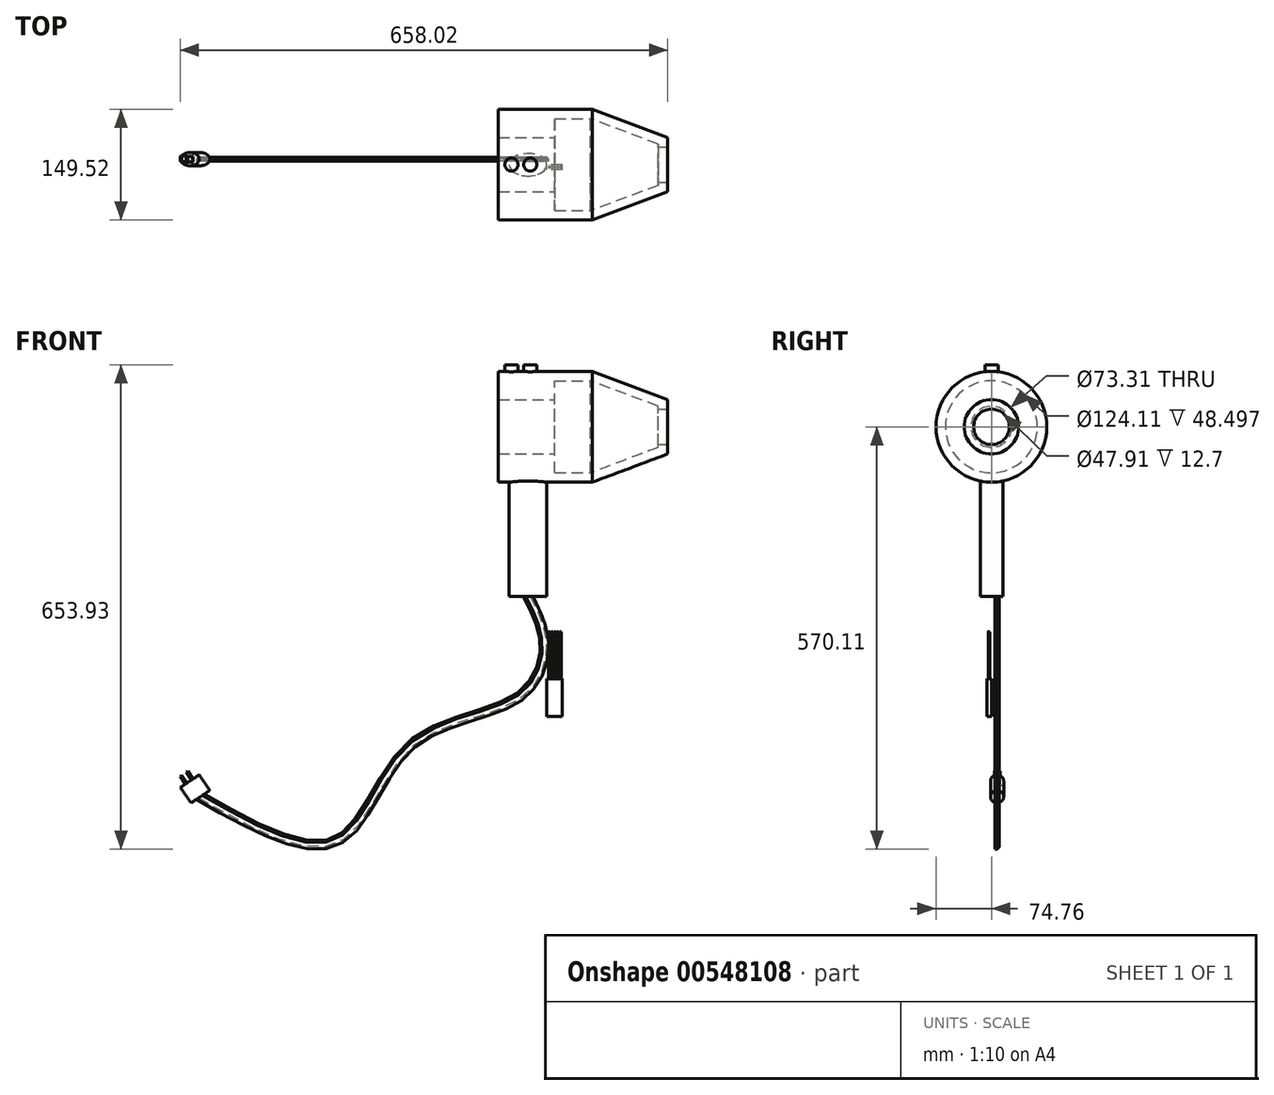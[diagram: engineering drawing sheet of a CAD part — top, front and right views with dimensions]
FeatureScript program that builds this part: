
annotation { "Feature Type Name" : "Feature", "Feature Type Description" : "" }
export const myFeature = defineFeature(function(context is Context, id is Id, definition is map)
    precondition{}
    {
        {
            var Q0;
            Q0=qCreatedBy(makeId("Front.planeOp"),FACE);
            var sketch = newSketch(context, id + "F0", { "sketchPlane" : qUnion([Q0])});
            skLineSegment(sketch, "E0", {"start": v(-65.57, 36.66) * mm, "end": v(-65.57, 74.76) * mm});
            skLineSegment(sketch, "E1", {"start": v(-65.57, 74.76) * mm, "end": v(61.43, 74.76) * mm});
            skLineSegment(sketch, "E2", {"start": v(61.43, 74.76) * mm, "end": v(163.03, 36.66) * mm});
            skLineSegment(sketch, "E3", {"start": v(163.03, 36.66) * mm, "end": v(163.03, 23.96) * mm});
            skLineSegment(sketch, "E4", {"start": v(163.03, 23.96) * mm, "end": v(150.33, 23.96) * mm});
            skLineSegment(sketch, "E5", {"start": v(150.33, 23.96) * mm, "end": v(150.33, 27.86) * mm});
            skLineSegment(sketch, "E6", {"start": v(150.33, 27.86) * mm, "end": v(59.13, 62.06) * mm});
            skLineSegment(sketch, "E7", {"start": v(59.13, 62.06) * mm, "end": v(10.63, 62.06) * mm});
            skLineSegment(sketch, "E8", {"start": v(10.63, 62.06) * mm, "end": v(10.63, 36.66) * mm});
            skLineSegment(sketch, "E9", {"start": v(10.63, 36.66) * mm, "end": v(-65.57, 36.66) * mm});
            skLineSegment(sketch, "E10", {"start": v(0, 0) * mm, "end": v(-123.38, 0) * mm, "construction": true});
            skSolve(sketch);
        }
        {
            var Q0;
            Q0=makeQuery(id+"F0.imprint","IMPRINT",FACE,{"disambiguationData":[TD([[makeQuery(id+"F0.imprint","IMPRINT",EDGE,{"derivedFrom":sQuery(id+"F0.wireOp",EDGE,"E0")}),-1.0]])]});
            var Q1;
            Q1=sQuery(id+"F0.wireOp",EDGE,"E10");
            revolve(context, id + "F1", {"entities" : qUnion([Q0]), "axis" : qUnion([Q1]), "revolveType" : RevolveType.FULL});
        }
        {
            var Q0;
            Q0=qCreatedBy(makeId("Top.planeOp"),FACE);
            cPlane(context, id + "F2", {"entities" : qUnion([Q0]), "cplaneType" : CPlaneType.OFFSET, "offset" : 50.8 * mm, "oppositeDirection" : true, "width" : 152.4 * mm, "height" : 152.4 * mm});
        }
        {
            var Q0;
            Q0=qCreatedBy(id+"F2.planeOp",FACE);
            var sketch = newSketch(context, id + "F3", { "sketchPlane" : qUnion([Q0])});
            skLineSegment(sketch, "E11", {"start": v(-43.6, 0) * mm, "end": v(0, 0) * mm});
            skEllipse(sketch, "E12", {"center": v(-25.4, 0) * mm, "majorRadius": 25.4 * mm, "minorRadius": 15.24 * mm, "majorAxis": v(1, 0)});
            skSolve(sketch);
        }
        {
            var Q0;
            Q0 = qSketchRegion(id + "F3", true);
            extrude(context, id + "F4", {"entities" : qUnion([Q0]), "operationType" : NewBodyOperationType.ADD, "oppositeDirection" : true, "depth" : 177.8 * mm, "offsetDistance" : 25.4 * mm});
        }
        {
            var Q0;
            Q0=makeQuery(id+"F4.opExtrude","CAP_FACE",FACE,{"disambiguationData":[OSD([sQuery(id+"F3.wireOp",EDGE,"E12")])],"isStart":false});
            var sketch = newSketch(context, id + "F5", { "sketchPlane" : qUnion([Q0])});
            skLineSegment(sketch, "E13", {"start": v(-7.37, -7.62) * mm, "end": v(-43.43, -7.62) * mm, "construction": true});
            skLineSegment(sketch, "E14.bottom", {"start": v(-31.75, -10.22) * mm, "end": v(-19.05, -10.22) * mm});
            skLineSegment(sketch, "E14.top", {"start": v(-31.75, -5.02) * mm, "end": v(-19.05, -5.02) * mm});
            skLineSegment(sketch, "E14.left", {"start": v(-31.75, -10.22) * mm, "end": v(-31.75, -5.02) * mm});
            skLineSegment(sketch, "E14.right", {"start": v(-19.05, -10.22) * mm, "end": v(-19.05, -5.02) * mm});
            skPoint(sketch, "E14.middle", {"position": v(-25.4, -7.62) * mm});
            skLineSegment(sketch, "E15", {"start": v(-50.8, 0) * mm, "end": v(0, 0) * mm, "construction": true});
            skLineSegment(sketch, "E16", {"start": v(-25.4, -15.24) * mm, "end": v(-25.4, 15.24) * mm, "construction": true});
            skEllipse(sketch, "E17", {"center": v(-25.4, -7.62) * mm, "majorRadius": 7.62 * mm, "minorRadius": 3.81 * mm, "majorAxis": v(0.9, 0.42)});
            skSolve(sketch);
        }
        {
            var Q0;
            Q0=qCreatedBy(makeId("Front.planeOp"),FACE);
            cPlane(context, id + "F6", {"entities" : qUnion([Q0]), "cplaneType" : CPlaneType.OFFSET, "offset" : 7.62 * mm, "oppositeDirection" : true, "width" : 152.4 * mm, "height" : 152.4 * mm});
        }
        {
            var Q0;
            Q0=qCreatedBy(id+"F6.planeOp",FACE);
            var sketch = newSketch(context, id + "F7", { "sketchPlane" : qUnion([Q0])});
            skFitSpline(sketch, "E18", {"points": [v(-25.4, -228.6) * mm, v(-3.46, -295.06) * mm, v(-38.9, -365.34) * mm, v(-184.15, -430.18) * mm, v(-282.57, -558.35) * mm, v(-467.83, -499.14) * mm], "startDerivative": vector(216.5, -432.15) * mm, "endDerivative": vector(-862.13, 491.31) * mm});
            skSolve(sketch);
        }
        {
            var Q0;
            Q0=makeQuery(id+"F5.imprint","IMPRINT",FACE,{"disambiguationData":[TD([[makeQuery(id+"F5.imprint","IMPRINT",EDGE,{"derivedFrom":sQuery(id+"F5.wireOp",EDGE,"E17")}),1.0]])]});
            var Q1;
            Q1=sQuery(id+"F7.wireOp",EDGE,"E18");
            sweep(context, id + "F8", {"operationType" : NewBodyOperationType.ADD, "profiles" : qUnion([Q0]), "path" : qUnion([Q1])});
        }
        {
            var Q0;
            Q0=makeQuery(id+"F8.opSweep","CAP_FACE",FACE,{"disambiguationData":[OSD([sQuery(id+"F5.wireOp",EDGE,"E14.bottom"),sQuery(id+"F5.wireOp",EDGE,"E14.top"),sQuery(id+"F5.wireOp",EDGE,"E14.left"),sQuery(id+"F5.wireOp",EDGE,"E14.right"),sQuery(id+"F5.wireOp",EDGE,"E17"),sQuery(id+"F7.wireOp",VERTEX,"E18.end")])],"isStart":false});
            var sketch = newSketch(context, id + "F9", { "sketchPlane" : qUnion([Q0])});
            skLineSegment(sketch, "E19", {"start": v(-659.83, 10.22) * mm, "end": v(-672.53, 5.02) * mm, "construction": true});
            skEllipse(sketch, "E20", {"center": v(-666.18, 7.62) * mm, "majorRadius": 15.24 * mm, "minorRadius": 8.9 * mm, "majorAxis": v(1, 0)});
            skSolve(sketch);
        }
        {
            var Q0;
            Q0 = qSketchRegion(id + "F9", true);
            extrude(context, id + "F10", {"entities" : qUnion([Q0]), "operationType" : NewBodyOperationType.ADD, "depth" : 25.4 * mm, "offsetDistance" : 25.4 * mm});
        }
        {
            var Q0;
            Q0=makeQuery(id+"F10.opExtrude","CAP_FACE",FACE,{"disambiguationData":[OSD([sQuery(id+"F9.wireOp",EDGE,"E20")])],"isStart":false});
            var sketch = newSketch(context, id + "F11", { "sketchPlane" : qUnion([Q0])});
            skLineSegment(sketch, "E21", {"start": v(-662.19, -11.56) * mm, "end": v(-662.19, 34.42) * mm});
            skLineSegment(sketch, "E22", {"start": v(-672.15, -14.27) * mm, "end": v(-672.15, 30.29) * mm});
            skLineSegment(sketch, "E23", {"start": v(-681.42, 7.62) * mm, "end": v(-655.08, 7.62) * mm});
            skLineSegment(sketch, "E24.bottom", {"start": v(-660.92, 3.81) * mm, "end": v(-663.46, 3.81) * mm});
            skLineSegment(sketch, "E24.top", {"start": v(-660.92, 11.43) * mm, "end": v(-663.46, 11.43) * mm});
            skLineSegment(sketch, "E24.left", {"start": v(-660.92, 3.81) * mm, "end": v(-660.92, 11.43) * mm});
            skLineSegment(sketch, "E24.right", {"start": v(-663.46, 3.81) * mm, "end": v(-663.46, 11.43) * mm});
            skPoint(sketch, "E24.middle", {"position": v(-662.19, 7.62) * mm});
            skLineSegment(sketch, "E25.bottom", {"start": v(-670.88, 4.2) * mm, "end": v(-673.42, 4.2) * mm});
            skLineSegment(sketch, "E25.top", {"start": v(-670.88, 11.82) * mm, "end": v(-673.42, 11.82) * mm});
            skLineSegment(sketch, "E25.left", {"start": v(-670.88, 4.2) * mm, "end": v(-670.88, 11.82) * mm});
            skLineSegment(sketch, "E25.right", {"start": v(-673.42, 4.2) * mm, "end": v(-673.42, 11.82) * mm});
            skPoint(sketch, "E25.middle", {"position": v(-672.15, 8) * mm});
            skSolve(sketch);
        }
        {
            var Q0;
            Q0 = qSketchRegion(id + "F11", true);
            var Q1;
            {var subQ0=sQuery(id+"F11.wireOp",EDGE,"E23");var subQ1=sQuery(id+"F11.wireOp",EDGE,"E21");var subQ2=makeQuery(id+"F11.imprint","INTERSECT",VERTEX,{"derivedFrom":[subQ1,subQ0]});Q1=makeQuery(id+"F11.imprint","IMPRINT",FACE,{"disambiguationData":[TD([[makeQuery(id+"F11.imprint","IMPRINT",EDGE,{"disambiguationData":[TD([[subQ2,-1.0]])],"derivedFrom":subQ1}),1.0]])]});}
            extrude(context, id + "F12", {"entities" : qUnion([Q0, Q1]), "operationType" : NewBodyOperationType.ADD, "depth" : 12.7 * mm, "offsetDistance" : 25.4 * mm});
        }
        {
            var Q0;
            Q0=qCreatedBy(makeId("Front.planeOp"),FACE);
            var sketch = newSketch(context, id + "F13", { "sketchPlane" : qUnion([Q0])});
            skLineSegment(sketch, "E26.bottom", {"start": v(20.72, -339.9) * mm, "end": v(-0.16, -339.9) * mm});
            skLineSegment(sketch, "E26.top", {"start": v(20.72, -390.79) * mm, "end": v(-0.16, -390.79) * mm});
            skLineSegment(sketch, "E26.left", {"start": v(20.72, -339.9) * mm, "end": v(20.72, -390.79) * mm});
            skLineSegment(sketch, "E26.right", {"start": v(-0.16, -339.9) * mm, "end": v(-0.16, -390.79) * mm});
            skPoint(sketch, "E26.middle", {"position": v(10.28, -365.34) * mm});
            skSolve(sketch);
        }
        {
            var Q0;
            Q0 = qSketchRegion(id + "F13", true);
            extrude(context, id + "F14", {"entities" : qUnion([Q0]), "depth" : 6.35 * mm, "offsetDistance" : 25.4 * mm});
        }
        {
            var Q0;
            Q0=makeQuery(id+"F14.opExtrude","SWEPT_FACE",FACE,{"disambiguationData":[OSD([sQuery(id+"F13.wireOp",EDGE,"E26.bottom")])]});
            var sketch = newSketch(context, id + "F15", { "sketchPlane" : qUnion([Q0])});
            skLineSegment(sketch, "E27", {"start": v(20.72, -3.18) * mm, "end": v(0, -3.18) * mm, "construction": true});
            skCircle(sketch, "E28", {"center": v(18.55, -3.18) * mm, "radius": 1.02 * mm});
            skCircle(sketch, "E29", {"center": v(14.74, -3.18) * mm, "radius": 1.02 * mm});
            skCircle(sketch, "E30", {"center": v(10.93, -3.18) * mm, "radius": 1.02 * mm});
            skCircle(sketch, "E31", {"center": v(7.12, -3.18) * mm, "radius": 1.02 * mm});
            skCircle(sketch, "E32", {"center": v(3.3, -3.18) * mm, "radius": 1.02 * mm});
            skSolve(sketch);
        }
        {
            var Q0;
            Q0 = qSketchRegion(id + "F15", true);
            extrude(context, id + "F16", {"entities" : qUnion([Q0]), "operationType" : NewBodyOperationType.ADD, "depth" : 63.5 * mm, "offsetDistance" : 25.4 * mm});
        }
        {
            var Q0;
            Q0=qCreatedBy(makeId("Top.planeOp"),FACE);
            cPlane(context, id + "F17", {"entities" : qUnion([Q0]), "cplaneType" : CPlaneType.OFFSET, "offset" : 63.5 * mm, "width" : 152.4 * mm, "height" : 152.4 * mm});
        }
        {
            var Q0;
            Q0=qCreatedBy(id+"F17.planeOp",FACE);
            var sketch = newSketch(context, id + "F18", { "sketchPlane" : qUnion([Q0])});
            skLineSegment(sketch, "E33", {"start": v(-47.79, 0.21) * mm, "end": v(21.4, 0.21) * mm, "construction": true});
            skCircle(sketch, "E34", {"center": v(-47.79, 0.21) * mm, "radius": 8.9 * mm});
            skCircle(sketch, "E35", {"center": v(-22.39, 0.21) * mm, "radius": 8.9 * mm});
            skSolve(sketch);
        }
        {
            var Q0;
            Q0 = qSketchRegion(id + "F18", true);
            extrude(context, id + "F19", {"entities" : qUnion([Q0]), "operationType" : NewBodyOperationType.ADD, "depth" : 20.32 * mm, "offsetDistance" : 25.4 * mm});
        }
    });
